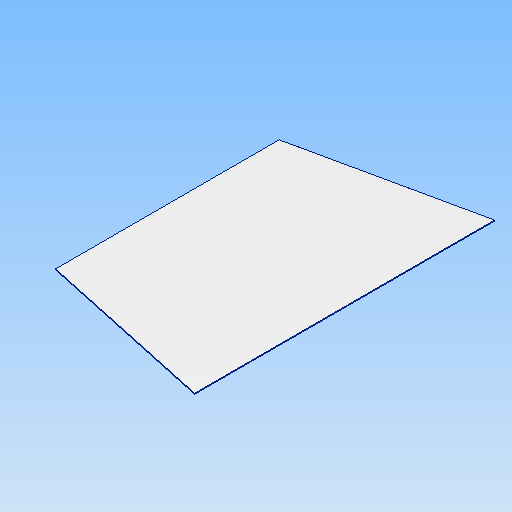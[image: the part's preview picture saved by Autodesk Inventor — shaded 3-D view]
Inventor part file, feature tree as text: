
AUTODESK INVENTOR PART (.ipt)
format: ipt  version: 2021 (Build 250183000, 183)  size: 81,408 bytes
history: native  units: in
note: dims shown in document units (in); Inventor stores cm internally (conversion verified against a paired STEP export)
features: extrude x1, sketch x1
ambient origin geometry x8: Origin, YZ Plane, XZ Plane, XY Plane, X Axis, Y Axis, Z Axis, Center Point
bodies: Solid1 (feature_tree)
feature tree (2):
  extrude  "Extrusion1"  [1 undecoded]
  sketch  "Sketch2"  dims[d8=0.063in d9=0.0in]
note: 1 required parameter value undecoded (feature->parameter linkage not recoverable at this tier; creation-order binding heuristic only, values carry confidence <= 0.55)
